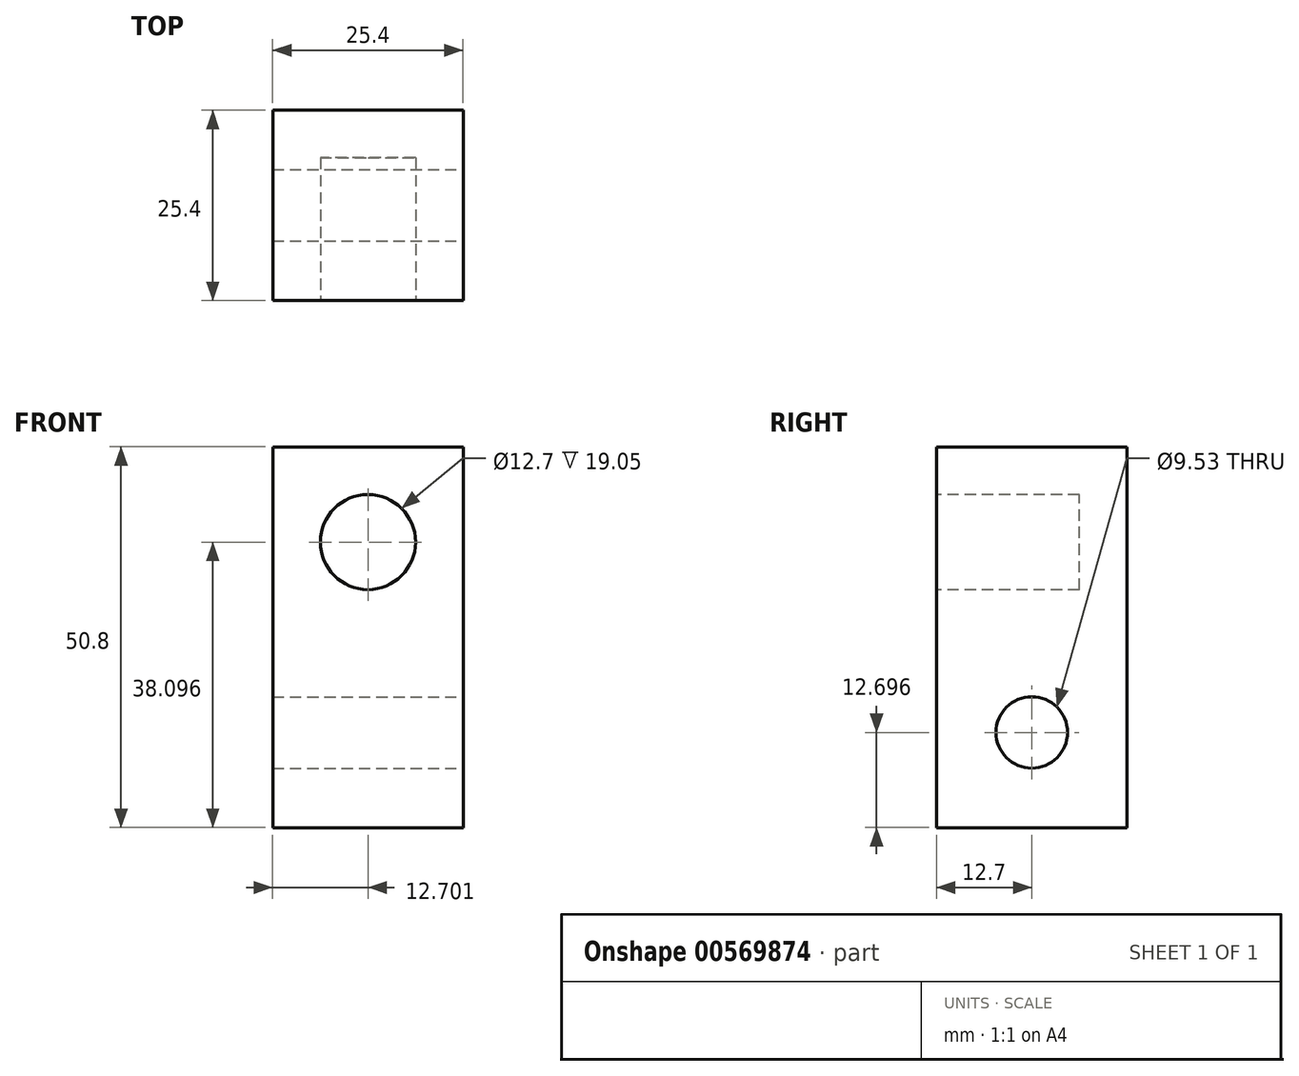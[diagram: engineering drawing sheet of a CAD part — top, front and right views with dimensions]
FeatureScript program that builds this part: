
annotation { "Feature Type Name" : "Feature", "Feature Type Description" : "" }
export const myFeature = defineFeature(function(context is Context, id is Id, definition is map)
    precondition{}
    {
        {
            var Q0;
            Q0=qCreatedBy(makeId("Front.planeOp"),FACE);
            var sketch = newSketch(context, id + "F0", { "sketchPlane" : qUnion([Q0])});
            skLineSegment(sketch, "E0.bottom", {"start": v(-25.66, -41.08) * mm, "end": v(-0.26, -41.08) * mm});
            skLineSegment(sketch, "E0.top", {"start": v(-25.66, 9.72) * mm, "end": v(-0.26, 9.72) * mm});
            skLineSegment(sketch, "E0.left", {"start": v(-25.66, -41.08) * mm, "end": v(-25.66, 9.72) * mm});
            skLineSegment(sketch, "E0.right", {"start": v(-0.26, -41.08) * mm, "end": v(-0.26, 9.72) * mm});
            skSolve(sketch);
        }
        {
            var Q0;
            Q0 = qSketchRegion(id + "F0", true);
            extrude(context, id + "F1", {"entities" : qUnion([Q0]), "depth" : 25.4 * mm, "offsetDistance" : 25.4 * mm});
        }
        {
            var Q0;
            Q0=makeQuery(id+"F1.opExtrude","CAP_FACE",FACE,{"disambiguationData":[OSD([sQuery(id+"F0.wireOp",EDGE,"E0.bottom"),sQuery(id+"F0.wireOp",EDGE,"E0.top"),sQuery(id+"F0.wireOp",EDGE,"E0.left"),sQuery(id+"F0.wireOp",EDGE,"E0.right")])],"isStart":false});
            var sketch = newSketch(context, id + "F2", { "sketchPlane" : qUnion([Q0])});
            skCircle(sketch, "E1", {"center": v(-12.96, -2.98) * mm, "radius": 6.35 * mm});
            skSolve(sketch);
        }
        {
            var Q0;
            Q0 = qSketchRegion(id + "F2", true);
            extrude(context, id + "F3", {"entities" : qUnion([Q0]), "operationType" : NewBodyOperationType.REMOVE, "oppositeDirection" : true, "depth" : 19.05 * mm, "offsetDistance" : 25.4 * mm});
        }
        {
            var Q0;
            Q0=makeQuery(id+"F1.opExtrude","SWEPT_FACE",FACE,{"disambiguationData":[OSD([sQuery(id+"F0.wireOp",EDGE,"E0.right")])]});
            var sketch = newSketch(context, id + "F4", { "sketchPlane" : qUnion([Q0])});
            skCircle(sketch, "E2", {"center": v(-12.7, -28.38) * mm, "radius": 4.76 * mm});
            skSolve(sketch);
        }
        {
            var Q0;
            Q0 = qSketchRegion(id + "F4", true);
            extrude(context, id + "F5", {"entities" : qUnion([Q0]), "operationType" : NewBodyOperationType.REMOVE, "oppositeDirection" : true, "depth" : 25.4 * mm, "offsetDistance" : 25.4 * mm});
        }
    });
